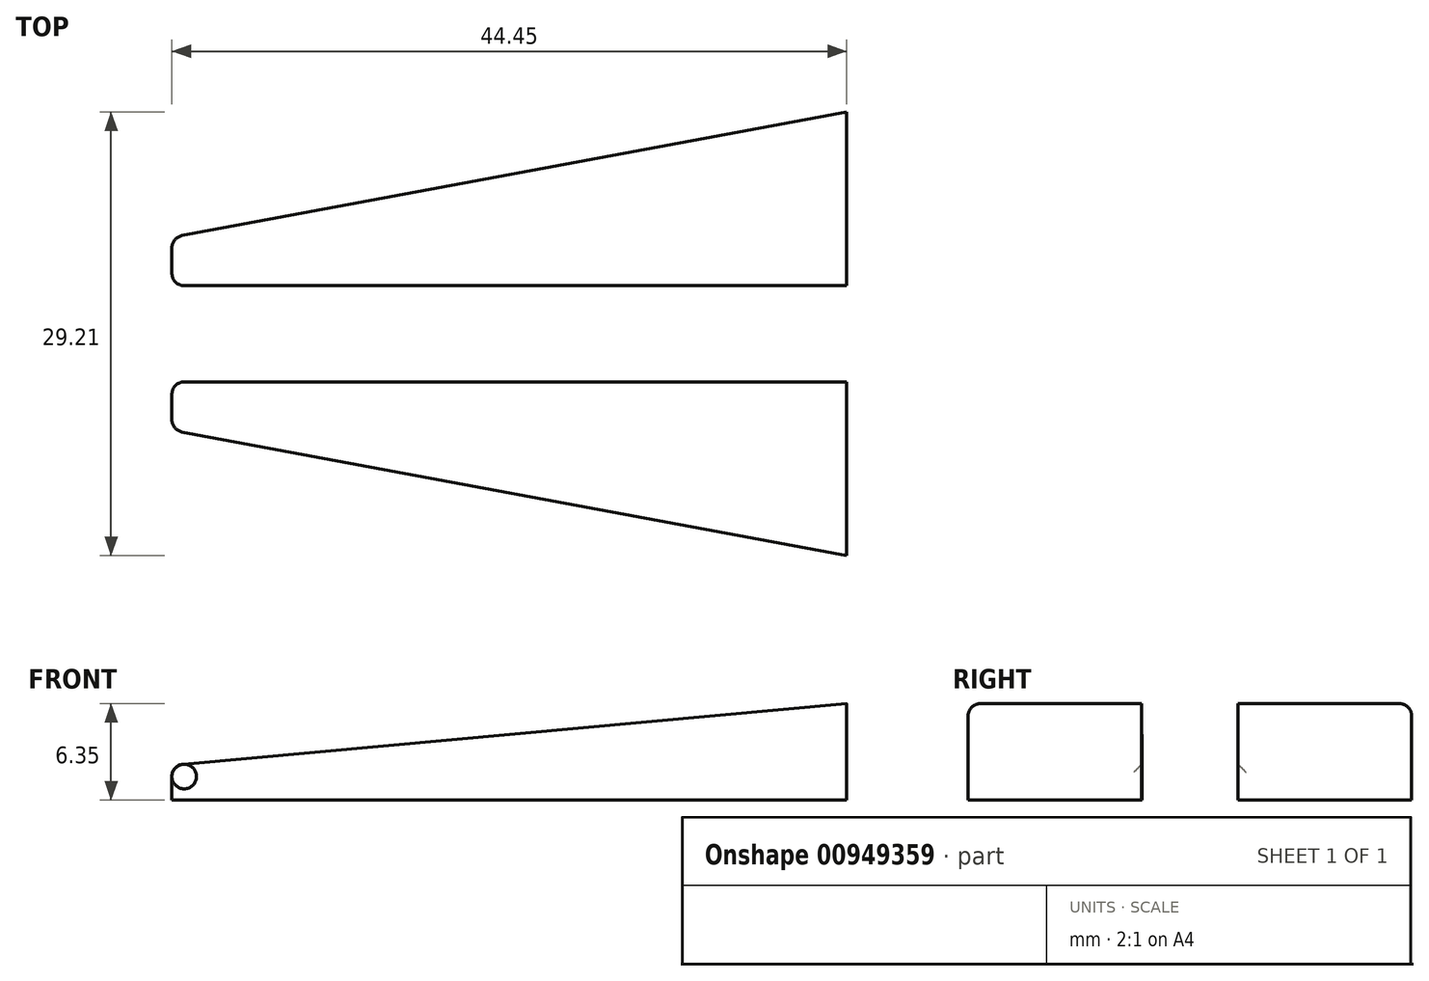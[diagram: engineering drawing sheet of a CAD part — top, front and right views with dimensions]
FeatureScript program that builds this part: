
annotation { "Feature Type Name" : "Feature", "Feature Type Description" : "" }
export const myFeature = defineFeature(function(context is Context, id is Id, definition is map)
    precondition{}
    {
        {
            var Q0;
            Q0=qCreatedBy(makeId("Top.planeOp"),FACE);
            var sketch = newSketch(context, id + "F0", { "sketchPlane" : qUnion([Q0])});
            skLineSegment(sketch, "E0.bottom", {"start": v(0, 0) * mm, "end": v(-44.45, -0.01) * mm});
            skLineSegment(sketch, "E0.left", {"start": v(0, 0) * mm, "end": v(0, 11.43) * mm});
            skLineSegment(sketch, "E0.right", {"start": v(-44.45, -0.01) * mm, "end": v(-44.45, 3.16) * mm});
            skLineSegment(sketch, "E1", {"start": v(0, 11.43) * mm, "end": v(-44.45, 3.16) * mm});
            skSolve(sketch);
        }
        {
            var Q0;
            Q0=makeQuery(id+"F0.imprint","IMPRINT",FACE,{"disambiguationData":[TD([[makeQuery(id+"F0.imprint","IMPRINT",EDGE,{"derivedFrom":sQuery(id+"F0.wireOp",EDGE,"E0.bottom")}),-1.0]])]});
            extrude(context, id + "F1", {"entities" : qUnion([Q0]), "depth" : 6.35 * mm, "offsetDistance" : 25.4 * mm});
        }
        {
            var Q0;
            Q0=makeQuery(id+"F1.opExtrude","SWEPT_FACE",FACE,{"disambiguationData":[OSD([sQuery(id+"F0.wireOp",EDGE,"E0.bottom")])]});
            var sketch = newSketch(context, id + "F2", { "sketchPlane" : qUnion([Q0])});
            skLineSegment(sketch, "E2", {"start": v(0, 6.35) * mm, "end": v(-44.45, 2.3) * mm});
            skLineSegment(sketch, "E3", {"start": v(-44.45, 2.3) * mm, "end": v(-57.36, 20.25) * mm});
            skLineSegment(sketch, "E4", {"start": v(-57.36, 20.25) * mm, "end": v(0, 6.35) * mm});
            skSolve(sketch);
        }
        {
            var Q0;
            {var subQ0=sQuery(id+"F2.wireOp",EDGE,"E2");Q0=makeQuery(id+"F2.imprint","IMPRINT",FACE,{"disambiguationData":[TD([[makeQuery(id+"F2.imprint","IMPRINT",EDGE,{"derivedFrom":subQ0}),-1.0]])]});}
            var Q1;
            {var subQ0=sQuery(id+"F2.wireOp",EDGE,"E3");Q1=makeQuery(id+"F2.imprint","IMPRINT",FACE,{"disambiguationData":[TD([[makeQuery(id+"F2.imprint","IMPRINT",EDGE,{"derivedFrom":subQ0}),-1.0]])]});}
            extrude(context, id + "F3", {"entities" : qUnion([Q0, Q1]), "operationType" : NewBodyOperationType.REMOVE, "oppositeDirection" : true, "depth" : 25.4 * mm, "offsetDistance" : 25.4 * mm});
        }
        {
            var Q0;
            Q0=makeQuery(id+"F1.opExtrude","SWEPT_EDGE",EDGE,{"disambiguationData":[OSD([sQuery(id+"F0.wireOp",EDGE,"E0.bottom"),sQuery(id+"F0.wireOp",EDGE,"E0.right")])]});
            var Q1;
            Q1=makeQuery(id+"F3.boolean.opBoolean","COPY",EDGE,{"derivedFrom":makeQuery(id+"F3.opExtrude","CAP_EDGE",EDGE,{"disambiguationData":[OSD([sQuery(id+"F2.wireOp",EDGE,"E2")])],"isStart":true})});
            var Q2;
            Q2=makeQuery(id+"F3.boolean.opBoolean","INTERSECT",EDGE,{"derivedFrom":[makeQuery(id+"F1.opExtrude","SWEPT_FACE",FACE,{"disambiguationData":[OSD([sQuery(id+"F0.wireOp",EDGE,"E1")])]}),makeQuery(id+"F3.opExtrude","SWEPT_FACE",FACE,{"disambiguationData":[OSD([sQuery(id+"F2.wireOp",EDGE,"E2")])]})]});
            var Q3;
            Q3=makeQuery(id+"F3.boolean.opBoolean","INTERSECT",EDGE,{"derivedFrom":[makeQuery(id+"F1.opExtrude","SWEPT_FACE",FACE,{"disambiguationData":[OSD([sQuery(id+"F0.wireOp",EDGE,"E0.right")])]}),makeQuery(id+"F3.opExtrude","SWEPT_FACE",FACE,{"disambiguationData":[OSD([sQuery(id+"F2.wireOp",EDGE,"E2")])]})]});
            var Q4;
            Q4=makeQuery(id+"F1.opExtrude","SWEPT_EDGE",EDGE,{"disambiguationData":[OSD([sQuery(id+"F0.wireOp",EDGE,"E0.right"),sQuery(id+"F0.wireOp",EDGE,"E1")])]});
            fillet(context, id + "F4", {"entities" : qUnion([Q0, Q1, Q2, Q3, Q4]), "radius" : 0.81 * mm, "tangentPropagation" : true, "allowEdgeOverflow" : false});
        }
        {
            var Q0;
            Q0=qCreatedBy(makeId("Front.planeOp"),FACE);
            cPlane(context, id + "F5", {"entities" : qUnion([Q0]), "cplaneType" : CPlaneType.OFFSET, "offset" : 3.17 * mm, "width" : 152.4 * mm, "height" : 152.4 * mm});
        }
        {
            var Q0;
            Q0=makeQuery(id+"F1.opExtrude","SWEPT_BODY",BODY,{"disambiguationData":[OSD([sQuery(id+"F0.wireOp",EDGE,"E0.bottom"),sQuery(id+"F0.wireOp",EDGE,"E0.left"),sQuery(id+"F0.wireOp",EDGE,"E0.right"),sQuery(id+"F0.wireOp",EDGE,"E1")])]});
            var Q1;
            Q1=qCreatedBy(id+"F5.planeOp",FACE);
            mirror(context, id + "F6", {"entities" : qUnion([Q0]), "mirrorPlane" : qUnion([Q1])});
        }
    });
